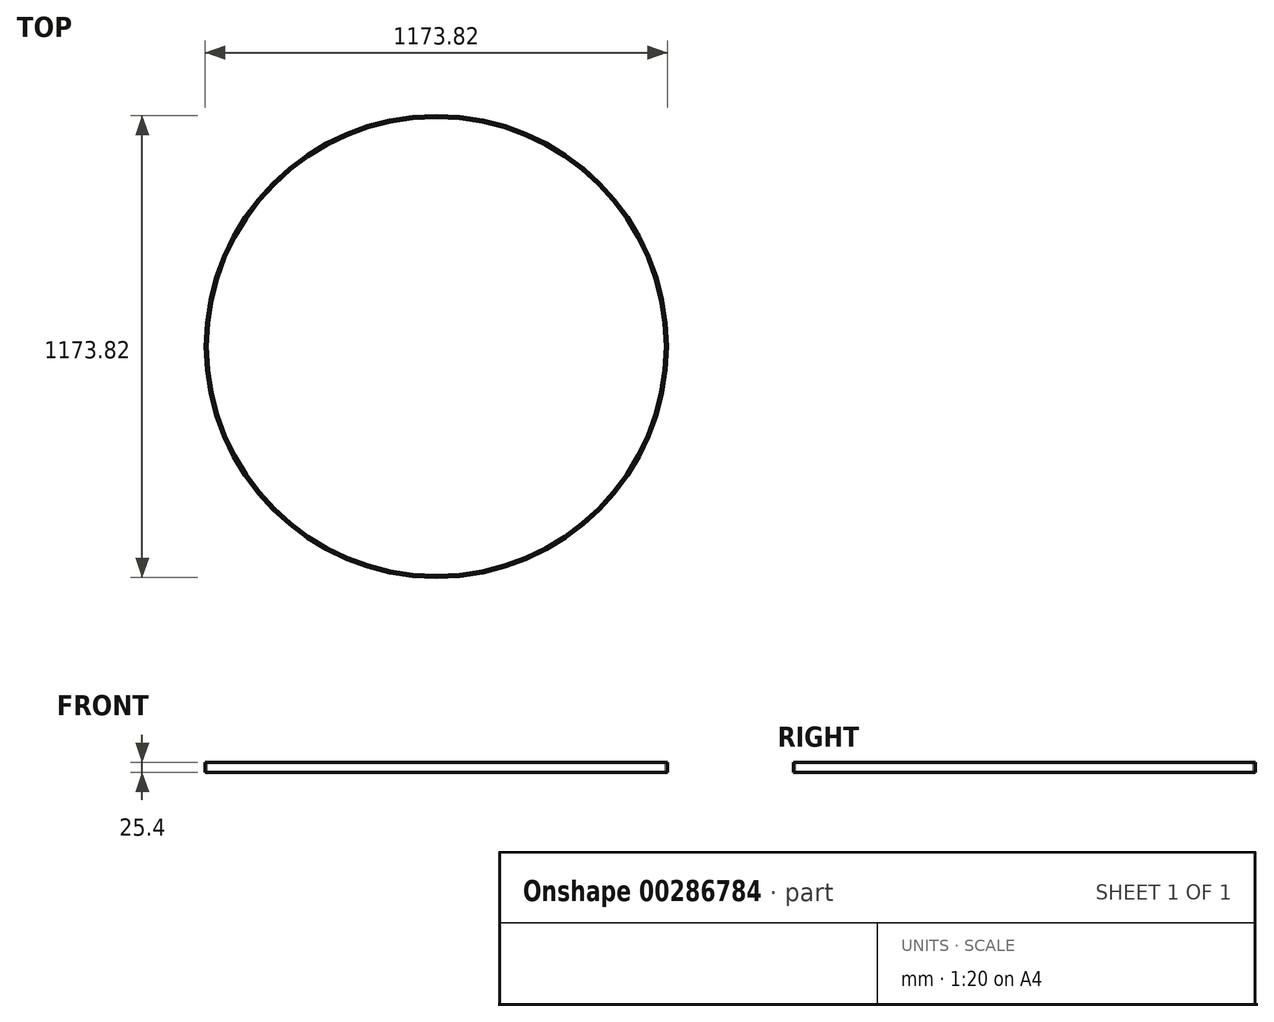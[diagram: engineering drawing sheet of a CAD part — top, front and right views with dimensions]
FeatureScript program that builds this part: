
annotation { "Feature Type Name" : "Feature", "Feature Type Description" : "" }
export const myFeature = defineFeature(function(context is Context, id is Id, definition is map)
    precondition{}
    {
        {
            var Q0;
            Q0=qCreatedBy(makeId("Top.planeOp"),FACE);
            var sketch = newSketch(context, id + "F0", { "sketchPlane" : qUnion([Q0])});
            skCircle(sketch, "E0", {"center": v(0, 0) * mm, "radius": 581.9 * mm});
            skCircle(sketch, "E1.0", {"center": v(0, 0) * mm, "radius": 583.9 * mm});
            skCircle(sketch, "E2.0", {"center": v(0, 0) * mm, "radius": 586.9 * mm});
            skSolve(sketch);
        }
        {
            var Q0;
            Q0=sQuery(id+"F0.wireOp",EDGE,"E2.0");
            var Q1;
            Q1=sQuery(id+"F0.wireOp",EDGE,"E1.0");
            var Q2;
            Q2=sQuery(id+"F0.wireOp",EDGE,"E0");
            extrude(context, id + "F1", {"bodyType" : ToolBodyType.SURFACE, "surfaceEntities" : qUnion([Q0, Q1, Q2]), "depth" : 25.4 * mm});
        }
    });
